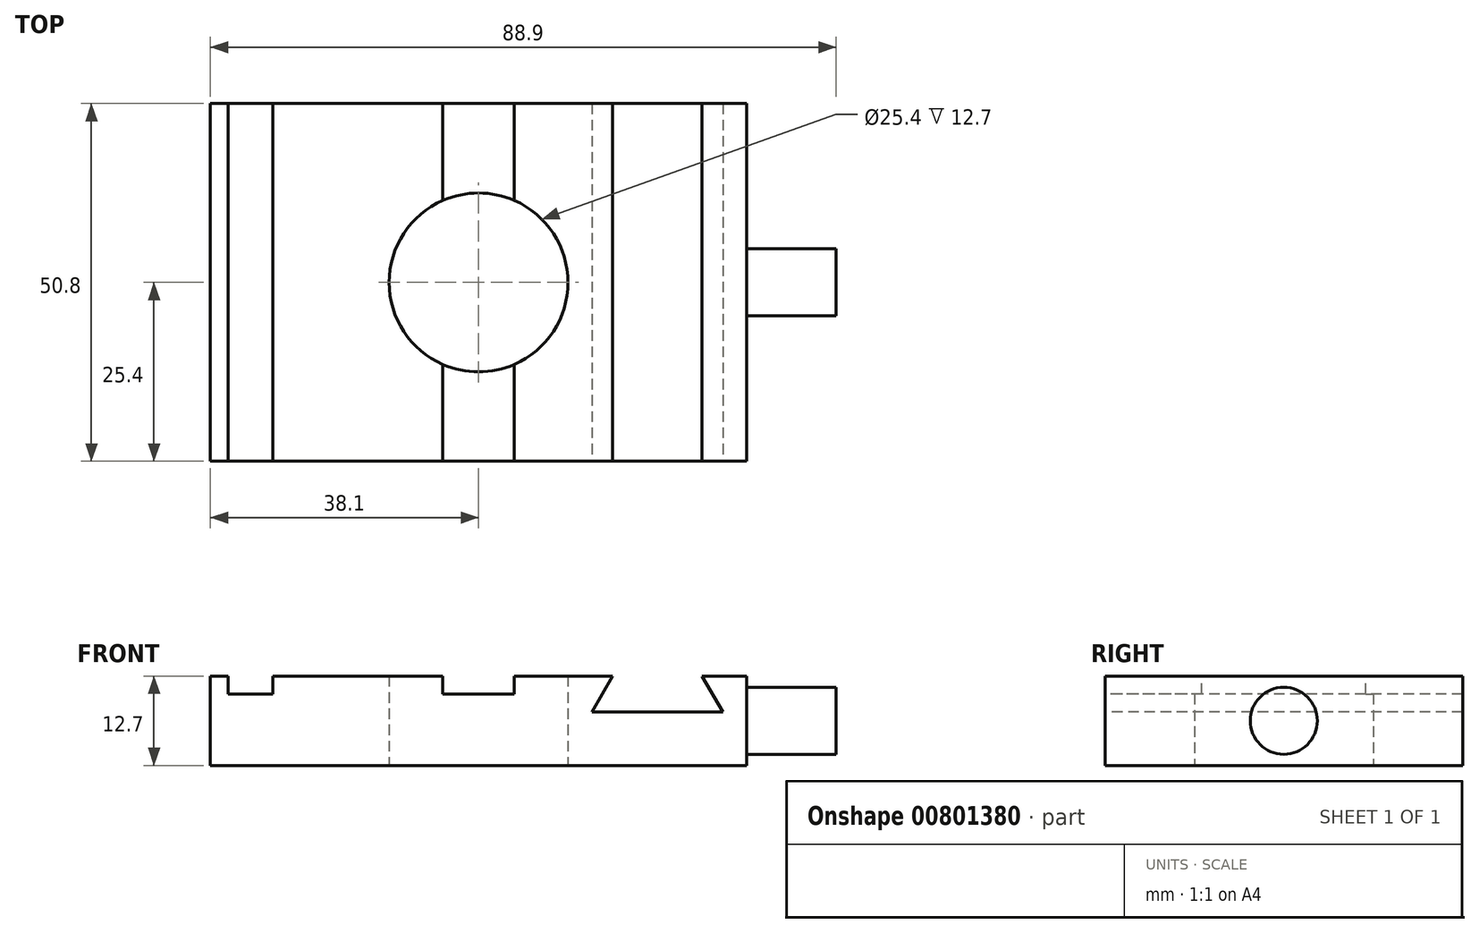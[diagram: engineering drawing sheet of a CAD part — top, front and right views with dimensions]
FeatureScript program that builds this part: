
annotation { "Feature Type Name" : "Feature", "Feature Type Description" : "" }
export const myFeature = defineFeature(function(context is Context, id is Id, definition is map)
    precondition{}
    {
        {
            var Q0;
            Q0=qCreatedBy(makeId("Top.planeOp"),FACE);
            var sketch = newSketch(context, id + "F0", { "sketchPlane" : qUnion([Q0])});
            skLineSegment(sketch, "E0.bottom", {"start": v(-38.1, -25.4) * mm, "end": v(38.1, -25.4) * mm});
            skLineSegment(sketch, "E0.top", {"start": v(-38.1, 25.4) * mm, "end": v(38.1, 25.4) * mm});
            skLineSegment(sketch, "E0.left", {"start": v(-38.1, -25.4) * mm, "end": v(-38.1, 25.4) * mm});
            skLineSegment(sketch, "E0.right", {"start": v(38.1, -25.4) * mm, "end": v(38.1, 25.4) * mm});
            skPoint(sketch, "E0.middle", {"position": v(0, 0) * mm});
            skCircle(sketch, "E1", {"center": v(0, 0) * mm, "radius": 12.7 * mm});
            skSolve(sketch);
        }
        {
            var Q0;
            Q0=makeQuery(id+"F0.imprint","IMPRINT",FACE,{"disambiguationData":[TD([[makeQuery(id+"F0.imprint","IMPRINT",EDGE,{"derivedFrom":sQuery(id+"F0.wireOp",EDGE,"E0.bottom")}),1.0]])]});
            extrude(context, id + "F1", {"entities" : qUnion([Q0]), "depth" : 12.7 * mm, "offsetDistance" : 25.4 * mm});
        }
        {
            var Q0;
            Q0=makeQuery(id+"F1.opExtrude","CAP_FACE",FACE,{"disambiguationData":[OSD([sQuery(id+"F0.wireOp",EDGE,"E0.bottom"),sQuery(id+"F0.wireOp",EDGE,"E0.top"),sQuery(id+"F0.wireOp",EDGE,"E0.left"),sQuery(id+"F0.wireOp",EDGE,"E0.right"),sQuery(id+"F0.wireOp",EDGE,"E1")])],"isStart":false});
            var sketch = newSketch(context, id + "F2", { "sketchPlane" : qUnion([Q0])});
            skLineSegment(sketch, "E2.bottom", {"start": v(-35.56, 25.4) * mm, "end": v(-29.21, 25.4) * mm});
            skLineSegment(sketch, "E2.top", {"start": v(-35.56, -25.4) * mm, "end": v(-29.21, -25.4) * mm});
            skLineSegment(sketch, "E2.left", {"start": v(-35.56, 25.4) * mm, "end": v(-35.56, -25.4) * mm});
            skLineSegment(sketch, "E2.right", {"start": v(-29.21, 25.4) * mm, "end": v(-29.21, -25.4) * mm});
            skLineSegment(sketch, "E3", {"start": v(-5.08, 25.4) * mm, "end": v(-5.08, -25.4) * mm});
            skLineSegment(sketch, "E4", {"start": v(-5.08, -25.4) * mm, "end": v(5.08, -25.4) * mm});
            skLineSegment(sketch, "E5", {"start": v(5.08, -25.4) * mm, "end": v(5.08, 25.4) * mm});
            skLineSegment(sketch, "E6", {"start": v(5.08, 25.4) * mm, "end": v(-5.08, 25.4) * mm});
            skPoint(sketch, "E7", {"position": v(0, 0) * mm});
            skLineSegment(sketch, "E8", {"start": v(0, 25.4) * mm, "end": v(0, -25.4) * mm, "construction": true});
            skSolve(sketch);
        }
        {
            var Q0;
            Q0=makeQuery(id+"F2.imprint","IMPRINT",FACE,{"disambiguationData":[TD([[makeQuery(id+"F2.imprint","IMPRINT",EDGE,{"derivedFrom":sQuery(id+"F2.wireOp",EDGE,"E2.bottom")}),-1.0]])]});
            var Q1;
            {var subQ0=sQuery(id+"F2.wireOp",EDGE,"E4");Q1=makeQuery(id+"F2.imprint","IMPRINT",FACE,{"disambiguationData":[TD([[makeQuery(id+"F2.imprint","IMPRINT",EDGE,{"derivedFrom":subQ0}),1.0]])]});}
            var Q2;
            {var subQ0=sQuery(id+"F2.wireOp",EDGE,"E6");Q2=makeQuery(id+"F2.imprint","IMPRINT",FACE,{"disambiguationData":[TD([[makeQuery(id+"F2.imprint","IMPRINT",EDGE,{"derivedFrom":subQ0}),-1.0]])]});}
            extrude(context, id + "F3", {"entities" : qUnion([Q0, Q1, Q2]), "operationType" : NewBodyOperationType.REMOVE, "oppositeDirection" : true, "depth" : 2.54 * mm, "offsetDistance" : 25.4 * mm});
        }
        {
            var Q0;
            Q0=makeQuery(id+"F1.opExtrude","SWEPT_FACE",FACE,{"disambiguationData":[OSD([sQuery(id+"F0.wireOp",EDGE,"E0.bottom")])]});
            var sketch = newSketch(context, id + "F4", { "sketchPlane" : qUnion([Q0])});
            skLineSegment(sketch, "E9", {"start": v(19.05, 12.7) * mm, "end": v(16.12, 7.62) * mm});
            skLineSegment(sketch, "E10", {"start": v(16.12, 7.62) * mm, "end": v(34.68, 7.62) * mm});
            skLineSegment(sketch, "E11", {"start": v(34.68, 7.62) * mm, "end": v(31.75, 12.7) * mm});
            skLineSegment(sketch, "E12", {"start": v(31.75, 12.7) * mm, "end": v(19.05, 12.7) * mm});
            skLineSegment(sketch, "E13", {"start": v(25.4, 12.7) * mm, "end": v(25.4, 7.62) * mm, "construction": true});
            skSolve(sketch);
        }
        {
            var Q0;
            Q0=makeQuery(id+"F4.imprint","IMPRINT",FACE,{"disambiguationData":[TD([[makeQuery(id+"F4.imprint","IMPRINT",EDGE,{"derivedFrom":sQuery(id+"F4.wireOp",EDGE,"E9")}),1.0]])]});
            extrude(context, id + "F5", {"entities" : qUnion([Q0]), "operationType" : NewBodyOperationType.REMOVE, "endBound" : BoundingType.THROUGH_ALL, "oppositeDirection" : true, "depth" : 25.4 * mm, "offsetDistance" : 25.4 * mm});
        }
        {
            var Q0;
            Q0=makeQuery(id+"F1.opExtrude","SWEPT_FACE",FACE,{"disambiguationData":[OSD([sQuery(id+"F0.wireOp",EDGE,"E0.right")])]});
            var sketch = newSketch(context, id + "F6", { "sketchPlane" : qUnion([Q0])});
            skCircle(sketch, "E14", {"center": v(0, 6.35) * mm, "radius": 4.76 * mm});
            skPoint(sketch, "E14.centerSnap0", {"position": v(-25.4, 6.35) * mm});
            skPoint(sketch, "E14.centerSnap1", {"position": v(0, 12.7) * mm});
            skSolve(sketch);
        }
        {
            var Q0;
            Q0=makeQuery(id+"F6.imprint","IMPRINT",FACE,{"disambiguationData":[TD([[makeQuery(id+"F6.imprint","IMPRINT",EDGE,{"derivedFrom":sQuery(id+"F6.wireOp",EDGE,"E14")}),1.0]])]});
            extrude(context, id + "F7", {"entities" : qUnion([Q0]), "operationType" : NewBodyOperationType.ADD, "depth" : 12.7 * mm, "offsetDistance" : 25.4 * mm});
        }
    });
